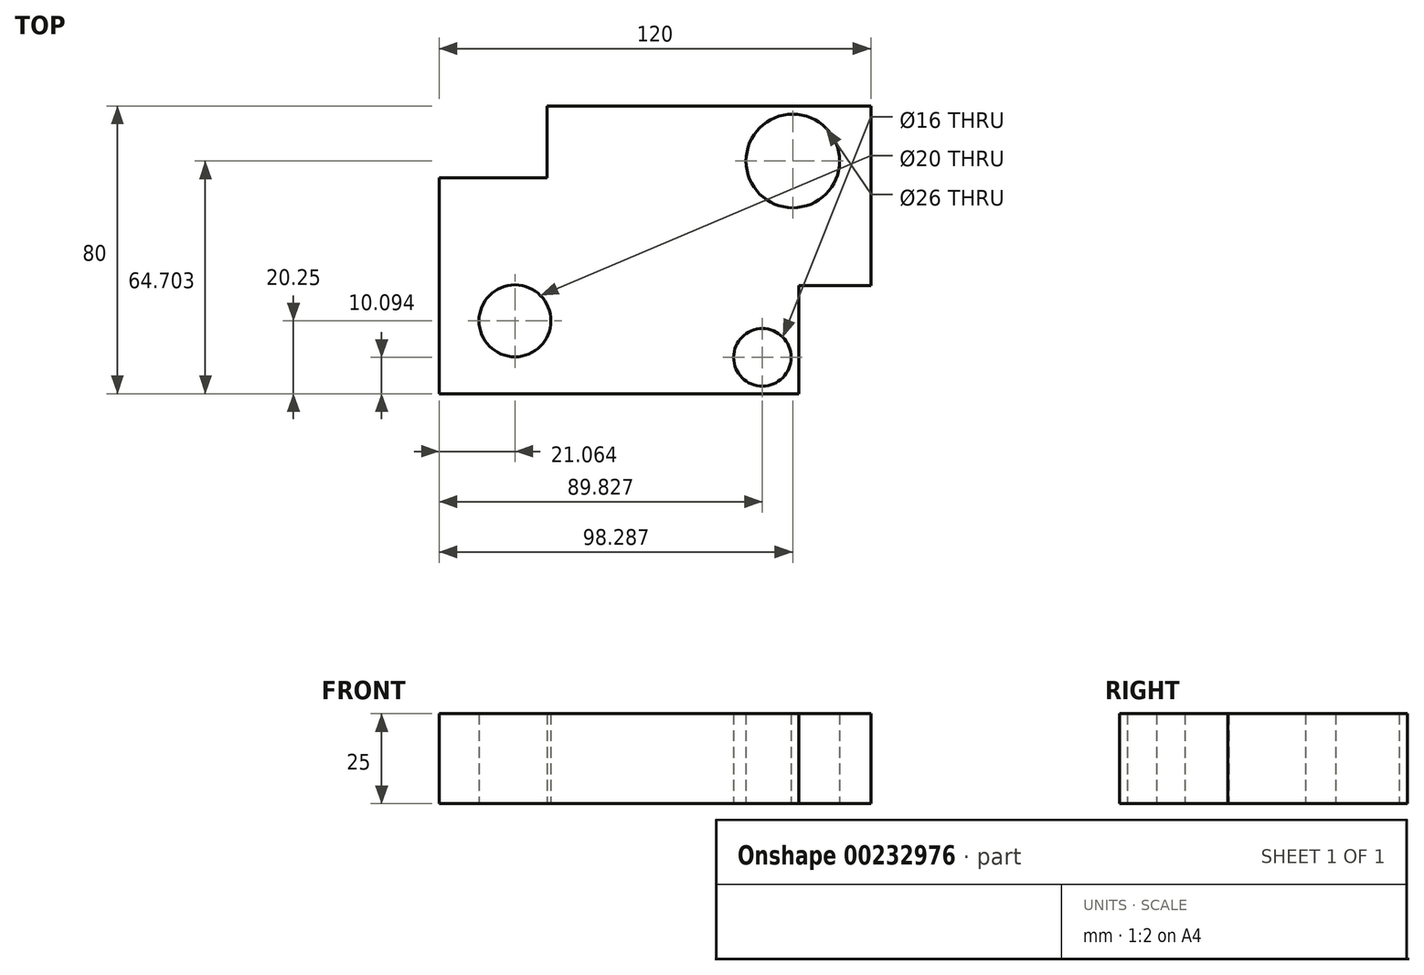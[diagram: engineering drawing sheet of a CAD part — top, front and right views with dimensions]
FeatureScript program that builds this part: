
annotation { "Feature Type Name" : "Feature", "Feature Type Description" : "" }
export const myFeature = defineFeature(function(context is Context, id is Id, definition is map)
    precondition{}
    {
        {
            var Q0;
            Q0=qCreatedBy(makeId("Top.planeOp"),FACE);
            var sketch = newSketch(context, id + "F0", { "sketchPlane" : qUnion([Q0])});
            skLineSegment(sketch, "E0", {"start": v(-44.7, 57.49) * mm, "end": v(45.3, 57.49) * mm});
            skLineSegment(sketch, "E1", {"start": v(45.3, 57.49) * mm, "end": v(45.3, 7.49) * mm});
            skLineSegment(sketch, "E2", {"start": v(45.3, 7.49) * mm, "end": v(25.3, 7.49) * mm});
            skLineSegment(sketch, "E3", {"start": v(25.3, 7.49) * mm, "end": v(25.3, -22.51) * mm});
            skLineSegment(sketch, "E4", {"start": v(25.3, -22.51) * mm, "end": v(-74.7, -22.51) * mm});
            skLineSegment(sketch, "E5", {"start": v(-74.7, -22.51) * mm, "end": v(-74.7, 37.49) * mm});
            skLineSegment(sketch, "E6", {"start": v(-44.7, 57.49) * mm, "end": v(-44.7, 37.49) * mm});
            skLineSegment(sketch, "E7", {"start": v(-44.7, 37.49) * mm, "end": v(-74.7, 37.49) * mm});
            skCircle(sketch, "E8", {"center": v(-53.64, -2.26) * mm, "radius": 10 * mm});
            skCircle(sketch, "E9", {"center": v(15.13, -12.42) * mm, "radius": 8 * mm});
            skCircle(sketch, "E10", {"center": v(23.59, 42.2) * mm, "radius": 13 * mm});
            skSolve(sketch);
        }
        {
            var Q0;
            Q0=makeQuery(id+"F0.imprint","IMPRINT",FACE,{"disambiguationData":[TD([[makeQuery(id+"F0.imprint","IMPRINT",EDGE,{"derivedFrom":sQuery(id+"F0.wireOp",EDGE,"E0")}),-1.0]])]});
            extrude(context, id + "F1", {"entities" : qUnion([Q0]), "depth" : 25 * mm});
        }
    });
